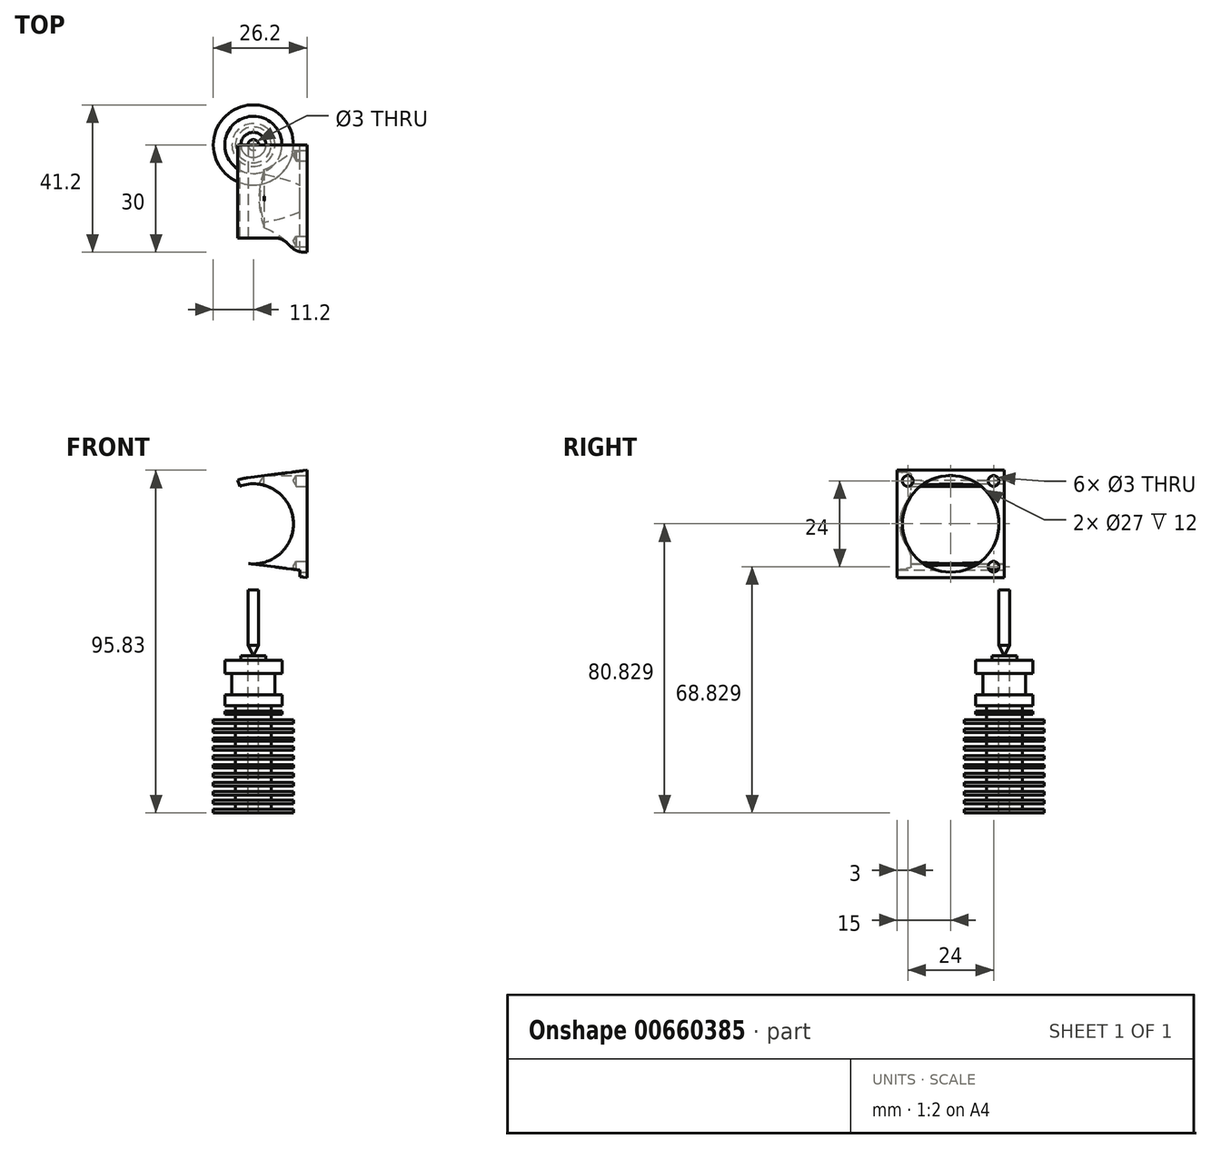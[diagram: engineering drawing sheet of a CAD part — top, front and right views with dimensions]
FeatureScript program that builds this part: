
annotation { "Feature Type Name" : "Feature", "Feature Type Description" : "" }
export const myFeature = defineFeature(function(context is Context, id is Id, definition is map)
    precondition{}
    {
        {
            var Q0;
            Q0=qCreatedBy(makeId("Front.planeOp"),FACE);
            var sketch = newSketch(context, id + "F0", { "sketchPlane" : qUnion([Q0])});
            skLineSegment(sketch, "E0.bottom", {"start": v(-3.5, 0) * mm, "end": v(3.5, 0) * mm});
            skLineSegment(sketch, "E0.top", {"start": v(-3.5, -1.2) * mm, "end": v(3.5, -1.2) * mm});
            skLineSegment(sketch, "E0.left", {"start": v(-3.5, 0) * mm, "end": v(-3.5, -1.2) * mm});
            skLineSegment(sketch, "E0.right", {"start": v(3.5, 0) * mm, "end": v(3.5, -1.2) * mm});
            skPoint(sketch, "E1", {"position": v(0, 0) * mm});
            skLineSegment(sketch, "E2", {"start": v(0, 5.65) * mm, "end": v(0, -51.62) * mm});
            skLineSegment(sketch, "E3.bottom", {"start": v(-8, -1.2) * mm, "end": v(8, -1.2) * mm});
            skLineSegment(sketch, "E3.top", {"start": v(-8, -4.9) * mm, "end": v(8, -4.9) * mm});
            skLineSegment(sketch, "E3.left", {"start": v(-8, -1.2) * mm, "end": v(-8, -4.9) * mm});
            skLineSegment(sketch, "E3.right", {"start": v(8, -1.2) * mm, "end": v(8, -4.9) * mm});
            skLineSegment(sketch, "E4.bottom", {"start": v(-8, -10.9) * mm, "end": v(8, -10.9) * mm});
            skLineSegment(sketch, "E4.top", {"start": v(-8, -13.9) * mm, "end": v(8, -13.9) * mm});
            skLineSegment(sketch, "E4.left", {"start": v(-8, -10.9) * mm, "end": v(-8, -13.9) * mm});
            skLineSegment(sketch, "E4.right", {"start": v(8, -10.9) * mm, "end": v(8, -13.9) * mm});
            skLineSegment(sketch, "E5.bottom", {"start": v(-6, -4.9) * mm, "end": v(6, -4.9) * mm});
            skLineSegment(sketch, "E5.top", {"start": v(-6, -10.9) * mm, "end": v(6, -10.9) * mm});
            skLineSegment(sketch, "E5.left", {"start": v(-6, -4.9) * mm, "end": v(-6, -10.9) * mm});
            skLineSegment(sketch, "E5.right", {"start": v(6, -4.9) * mm, "end": v(6, -10.9) * mm});
            skLineSegment(sketch, "E6.bottom", {"start": v(-11.2, -17.9) * mm, "end": v(11.2, -17.9) * mm});
            skLineSegment(sketch, "E6.top", {"start": v(-11.2, -18.9) * mm, "end": v(11.2, -18.9) * mm});
            skLineSegment(sketch, "E6.left", {"start": v(-11.2, -17.9) * mm, "end": v(-11.2, -18.9) * mm});
            skLineSegment(sketch, "E6.right", {"start": v(11.2, -17.9) * mm, "end": v(11.2, -18.9) * mm});
            skLineSegment(sketch, "E7.bottom", {"start": v(-8, -15.4) * mm, "end": v(8, -15.4) * mm});
            skLineSegment(sketch, "E7.top", {"start": v(-8, -16.4) * mm, "end": v(8, -16.4) * mm});
            skLineSegment(sketch, "E7.left", {"start": v(-8, -15.4) * mm, "end": v(-8, -16.4) * mm});
            skLineSegment(sketch, "E7.right", {"start": v(8, -15.4) * mm, "end": v(8, -16.4) * mm});
            skLineSegment(sketch, "E8.bottom", {"start": v(-5, -16.4) * mm, "end": v(5, -16.4) * mm});
            skLineSegment(sketch, "E8.top", {"start": v(-5, -43.9) * mm, "end": v(5, -43.9) * mm});
            skLineSegment(sketch, "E8.left", {"start": v(-5, -16.4) * mm, "end": v(-5, -43.9) * mm});
            skLineSegment(sketch, "E8.right", {"start": v(5, -16.4) * mm, "end": v(5, -43.9) * mm});
            skLineSegment(sketch, "E9.bottom", {"start": v(-5, -13.9) * mm, "end": v(5, -13.9) * mm});
            skLineSegment(sketch, "E9.top", {"start": v(-5, -15.4) * mm, "end": v(5, -15.4) * mm});
            skLineSegment(sketch, "E9.left", {"start": v(-5, -13.9) * mm, "end": v(-5, -15.4) * mm});
            skLineSegment(sketch, "E9.right", {"start": v(5, -13.9) * mm, "end": v(5, -15.4) * mm});
            skLineSegment(sketch, "E10", {"start": v(-23.04, -43.9) * mm, "end": v(22.42, -43.9) * mm, "construction": true});
            skLineSegment(sketch, "E11.bottom", {"start": v(-11.2, -42.9) * mm, "end": v(11.2, -42.9) * mm});
            skLineSegment(sketch, "E11.top", {"start": v(-11.2, -43.9) * mm, "end": v(11.2, -43.9) * mm});
            skLineSegment(sketch, "E11.left", {"start": v(-11.2, -42.9) * mm, "end": v(-11.2, -43.9) * mm});
            skLineSegment(sketch, "E11.right", {"start": v(11.2, -42.9) * mm, "end": v(11.2, -43.9) * mm});
            skLineSegment(sketch, "E12.bottom", {"start": v(-11.2, -40.4) * mm, "end": v(11.2, -40.4) * mm});
            skLineSegment(sketch, "E12.top", {"start": v(-11.2, -41.4) * mm, "end": v(11.2, -41.4) * mm});
            skLineSegment(sketch, "E12.left", {"start": v(-11.2, -40.4) * mm, "end": v(-11.2, -41.4) * mm});
            skLineSegment(sketch, "E12.right", {"start": v(11.2, -40.4) * mm, "end": v(11.2, -41.4) * mm});
            skLineSegment(sketch, "E13.bottom", {"start": v(-11.2, -37.9) * mm, "end": v(11.2, -37.9) * mm});
            skLineSegment(sketch, "E13.top", {"start": v(-11.2, -38.9) * mm, "end": v(11.2, -38.9) * mm});
            skLineSegment(sketch, "E13.left", {"start": v(-11.2, -37.9) * mm, "end": v(-11.2, -38.9) * mm});
            skLineSegment(sketch, "E13.right", {"start": v(11.2, -37.9) * mm, "end": v(11.2, -38.9) * mm});
            skLineSegment(sketch, "E14.bottom", {"start": v(-11.2, -35.4) * mm, "end": v(11.2, -35.4) * mm});
            skLineSegment(sketch, "E14.top", {"start": v(-11.2, -36.4) * mm, "end": v(11.2, -36.4) * mm});
            skLineSegment(sketch, "E14.left", {"start": v(-11.2, -35.4) * mm, "end": v(-11.2, -36.4) * mm});
            skLineSegment(sketch, "E14.right", {"start": v(11.2, -35.4) * mm, "end": v(11.2, -36.4) * mm});
            skLineSegment(sketch, "E15.bottom", {"start": v(-11.2, -32.9) * mm, "end": v(11.2, -32.9) * mm});
            skLineSegment(sketch, "E15.top", {"start": v(-11.2, -33.9) * mm, "end": v(11.2, -33.9) * mm});
            skLineSegment(sketch, "E15.left", {"start": v(-11.2, -32.9) * mm, "end": v(-11.2, -33.9) * mm});
            skLineSegment(sketch, "E15.right", {"start": v(11.2, -32.9) * mm, "end": v(11.2, -33.9) * mm});
            skLineSegment(sketch, "E16.bottom", {"start": v(-11.2, -30.4) * mm, "end": v(11.2, -30.4) * mm});
            skLineSegment(sketch, "E16.top", {"start": v(-11.2, -31.4) * mm, "end": v(11.2, -31.4) * mm});
            skLineSegment(sketch, "E16.left", {"start": v(-11.2, -30.4) * mm, "end": v(-11.2, -31.4) * mm});
            skLineSegment(sketch, "E16.right", {"start": v(11.2, -30.4) * mm, "end": v(11.2, -31.4) * mm});
            skLineSegment(sketch, "E17.bottom", {"start": v(-11.2, -27.9) * mm, "end": v(11.2, -27.9) * mm});
            skLineSegment(sketch, "E17.top", {"start": v(-11.2, -28.9) * mm, "end": v(11.2, -28.9) * mm});
            skLineSegment(sketch, "E17.left", {"start": v(-11.2, -27.9) * mm, "end": v(-11.2, -28.9) * mm});
            skLineSegment(sketch, "E17.right", {"start": v(11.2, -27.9) * mm, "end": v(11.2, -28.9) * mm});
            skLineSegment(sketch, "E18.bottom", {"start": v(-11.2, -25.4) * mm, "end": v(11.2, -25.4) * mm});
            skLineSegment(sketch, "E18.top", {"start": v(-11.2, -26.4) * mm, "end": v(11.2, -26.4) * mm});
            skLineSegment(sketch, "E18.left", {"start": v(-11.2, -25.4) * mm, "end": v(-11.2, -26.4) * mm});
            skLineSegment(sketch, "E18.right", {"start": v(11.2, -25.4) * mm, "end": v(11.2, -26.4) * mm});
            skLineSegment(sketch, "E19.bottom", {"start": v(-11.2, -22.9) * mm, "end": v(11.2, -22.9) * mm});
            skLineSegment(sketch, "E19.top", {"start": v(-11.2, -23.9) * mm, "end": v(11.2, -23.9) * mm});
            skLineSegment(sketch, "E19.left", {"start": v(-11.2, -22.9) * mm, "end": v(-11.2, -23.9) * mm});
            skLineSegment(sketch, "E19.right", {"start": v(11.2, -22.9) * mm, "end": v(11.2, -23.9) * mm});
            skLineSegment(sketch, "E20.bottom", {"start": v(-11.2, -20.4) * mm, "end": v(11.2, -20.4) * mm});
            skLineSegment(sketch, "E20.top", {"start": v(-11.2, -21.4) * mm, "end": v(11.2, -21.4) * mm});
            skLineSegment(sketch, "E20.left", {"start": v(-11.2, -20.4) * mm, "end": v(-11.2, -21.4) * mm});
            skLineSegment(sketch, "E20.right", {"start": v(11.2, -20.4) * mm, "end": v(11.2, -21.4) * mm});
            skLineSegment(sketch, "E21.bottom", {"start": v(29.22, -43.9) * mm, "end": v(59.22, -43.9) * mm});
            skLineSegment(sketch, "E21.top", {"start": v(29.22, -13.9) * mm, "end": v(59.22, -13.9) * mm});
            skLineSegment(sketch, "E21.left", {"start": v(29.22, -43.9) * mm, "end": v(29.22, -13.9) * mm});
            skLineSegment(sketch, "E21.right", {"start": v(59.22, -43.9) * mm, "end": v(59.22, -13.9) * mm});
            skLineSegment(sketch, "E22", {"start": v(87.52, -43.9) * mm, "end": v(112.52, -43.9) * mm});
            skLineSegment(sketch, "E23", {"start": v(112.52, -43.9) * mm, "end": v(112.52, -13.9) * mm});
            skLineSegment(sketch, "E24", {"start": v(112.52, -13.9) * mm, "end": v(102.52, -13.9) * mm});
            skLineSegment(sketch, "E25", {"start": v(102.52, -13.9) * mm, "end": v(102.52, -17.9) * mm});
            skLineSegment(sketch, "E26", {"start": v(102.52, -17.9) * mm, "end": v(87.52, -17.9) * mm});
            skLineSegment(sketch, "E27", {"start": v(87.52, -17.9) * mm, "end": v(87.52, -43.9) * mm});
            skCircle(sketch, "E28", {"center": v(0, 36.93) * mm, "radius": 11.2 * mm, "construction": true});
            skCircle(sketch, "E29", {"center": v(0, 36.93) * mm, "radius": 13 * mm, "construction": true});
            skLineSegment(sketch, "E30.right", {"start": v(25, 21.93) * mm, "end": v(25, 51.93) * mm});
            skLineSegment(sketch, "E31.right", {"start": v(15, 21.93) * mm, "end": v(15, 51.93) * mm});
            skLineSegment(sketch, "E32", {"start": v(15, 51.93) * mm, "end": v(-1.63, 49.83) * mm});
            skLineSegment(sketch, "E33", {"start": v(15, 21.93) * mm, "end": v(-1.63, 24.03) * mm});
            skLineSegment(sketch, "E34", {"start": v(15, 21.93) * mm, "end": v(25, 21.93) * mm});
            skLineSegment(sketch, "E35", {"start": v(15, 51.93) * mm, "end": v(25, 51.93) * mm});
            skLineSegment(sketch, "E36", {"start": v(0, 36.93) * mm, "end": v(-4.45, 49.15) * mm});
            skArc(sketch, "E37", {"start": v(-1.63, 49.83) * mm, "mid": v(-3.06, 49.56) * mm, "end": v(-4.45, 49.15) * mm});
            skPoint(sketch, "E38", {"position": v(15, 50.13) * mm});
            skPoint(sketch, "E39", {"position": v(15, 23.73) * mm});
            skLineSegment(sketch, "E40", {"start": v(15, 23.73) * mm, "end": v(-1.41, 25.82) * mm});
            skLineSegment(sketch, "E41", {"start": v(15, 50.13) * mm, "end": v(-1.41, 48.04) * mm});
            skLineSegment(sketch, "E42", {"start": v(0, 36.93) * mm, "end": v(-4.45, 24.71) * mm});
            skArc(sketch, "E43", {"start": v(-3.83, 47.45) * mm, "mid": v(11.2, 36.93) * mm, "end": v(-3.83, 26.4) * mm});
            skArc(sketch, "E44", {"start": v(-1.63, 24.03) * mm, "mid": v(-3.06, 24.3) * mm, "end": v(-4.45, 24.71) * mm});
            skLineSegment(sketch, "E45", {"start": v(0, 36.93) * mm, "end": v(33.8, 36.93) * mm, "construction": true});
            skLineSegment(sketch, "E46", {"start": v(13, 51.68) * mm, "end": v(13, 22.18) * mm});
            skSolve(sketch);
        }
        {
            var Q0;
            {var subQ0=sQuery(id+"F0.wireOp",EDGE,"E3.left");Q0=makeQuery(id+"F0.imprint","IMPRINT",FACE,{"disambiguationData":[TD([[makeQuery(id+"F0.imprint","IMPRINT",EDGE,{"derivedFrom":subQ0}),1.0]])]});}
            var Q1;
            {var subQ0=sQuery(id+"F0.wireOp",EDGE,"E0.left");Q1=makeQuery(id+"F0.imprint","IMPRINT",FACE,{"disambiguationData":[TD([[makeQuery(id+"F0.imprint","IMPRINT",EDGE,{"derivedFrom":subQ0}),1.0]])]});}
            var Q2;
            {var subQ5=sQuery(id+"F0.wireOp",EDGE,"E5.left");Q2=makeQuery(id+"F0.imprint","IMPRINT",FACE,{"disambiguationData":[TD([[makeQuery(id+"F0.imprint","IMPRINT",EDGE,{"derivedFrom":subQ5}),1.0]])]});}
            var Q3;
            {var subQ0=sQuery(id+"F0.wireOp",EDGE,"E4.left");Q3=makeQuery(id+"F0.imprint","IMPRINT",FACE,{"disambiguationData":[TD([[makeQuery(id+"F0.imprint","IMPRINT",EDGE,{"derivedFrom":subQ0}),1.0]])]});}
            var Q4;
            {var subQ5=sQuery(id+"F0.wireOp",EDGE,"E9.left");Q4=makeQuery(id+"F0.imprint","IMPRINT",FACE,{"disambiguationData":[TD([[makeQuery(id+"F0.imprint","IMPRINT",EDGE,{"derivedFrom":subQ5}),1.0]])]});}
            var Q5;
            {var subQ0=sQuery(id+"F0.wireOp",EDGE,"E7.left");Q5=makeQuery(id+"F0.imprint","IMPRINT",FACE,{"disambiguationData":[TD([[makeQuery(id+"F0.imprint","IMPRINT",EDGE,{"derivedFrom":subQ0}),1.0]])]});}
            var Q6;
            {var subQ0=sQuery(id+"F0.wireOp",EDGE,"E8.bottom");var subQ1=sQuery(id+"F0.wireOp",EDGE,"E2");var subQ2=makeQuery(id+"F0.imprint","INTERSECT",VERTEX,{"derivedFrom":[subQ1,subQ0]});Q6=makeQuery(id+"F0.imprint","IMPRINT",FACE,{"disambiguationData":[TD([[makeQuery(id+"F0.imprint","IMPRINT",EDGE,{"disambiguationData":[TD([[subQ2,-1.0]])],"derivedFrom":subQ1}),-1.0]])]});}
            var Q7;
            {var subQ0=sQuery(id+"F0.wireOp",EDGE,"E6.bottom");var subQ1=sQuery(id+"F0.wireOp",EDGE,"E2");var subQ2=makeQuery(id+"F0.imprint","INTERSECT",VERTEX,{"derivedFrom":[subQ1,subQ0]});Q7=makeQuery(id+"F0.imprint","IMPRINT",FACE,{"disambiguationData":[TD([[makeQuery(id+"F0.imprint","IMPRINT",EDGE,{"disambiguationData":[TD([[subQ2,-1.0]])],"derivedFrom":subQ1}),-1.0]])]});}
            var Q8;
            {var subQ0=sQuery(id+"F0.wireOp",EDGE,"E6.top");var subQ1=sQuery(id+"F0.wireOp",EDGE,"E2");var subQ2=makeQuery(id+"F0.imprint","INTERSECT",VERTEX,{"derivedFrom":[subQ1,subQ0]});Q8=makeQuery(id+"F0.imprint","IMPRINT",FACE,{"disambiguationData":[TD([[makeQuery(id+"F0.imprint","IMPRINT",EDGE,{"disambiguationData":[TD([[subQ2,-1.0]])],"derivedFrom":subQ1}),-1.0]])]});}
            var Q9;
            {var subQ0=sQuery(id+"F0.wireOp",EDGE,"E20.bottom");var subQ1=sQuery(id+"F0.wireOp",EDGE,"E2");var subQ2=makeQuery(id+"F0.imprint","INTERSECT",VERTEX,{"derivedFrom":[subQ1,subQ0]});Q9=makeQuery(id+"F0.imprint","IMPRINT",FACE,{"disambiguationData":[TD([[makeQuery(id+"F0.imprint","IMPRINT",EDGE,{"disambiguationData":[TD([[subQ2,-1.0]])],"derivedFrom":subQ1}),-1.0]])]});}
            var Q10;
            {var subQ0=sQuery(id+"F0.wireOp",EDGE,"E19.bottom");var subQ1=sQuery(id+"F0.wireOp",EDGE,"E2");var subQ2=makeQuery(id+"F0.imprint","INTERSECT",VERTEX,{"derivedFrom":[subQ1,subQ0]});Q10=makeQuery(id+"F0.imprint","IMPRINT",FACE,{"disambiguationData":[TD([[makeQuery(id+"F0.imprint","IMPRINT",EDGE,{"disambiguationData":[TD([[subQ2,-1.0]])],"derivedFrom":subQ1}),-1.0]])]});}
            var Q11;
            {var subQ5=sQuery(id+"F0.wireOp",EDGE,"E20.left");Q11=makeQuery(id+"F0.imprint","IMPRINT",FACE,{"disambiguationData":[TD([[makeQuery(id+"F0.imprint","IMPRINT",EDGE,{"derivedFrom":subQ5}),1.0]])]});}
            var Q12;
            {var subQ5=sQuery(id+"F0.wireOp",EDGE,"E19.left");Q12=makeQuery(id+"F0.imprint","IMPRINT",FACE,{"disambiguationData":[TD([[makeQuery(id+"F0.imprint","IMPRINT",EDGE,{"derivedFrom":subQ5}),1.0]])]});}
            var Q13;
            {var subQ5=sQuery(id+"F0.wireOp",EDGE,"E18.left");Q13=makeQuery(id+"F0.imprint","IMPRINT",FACE,{"disambiguationData":[TD([[makeQuery(id+"F0.imprint","IMPRINT",EDGE,{"derivedFrom":subQ5}),1.0]])]});}
            var Q14;
            {var subQ5=sQuery(id+"F0.wireOp",EDGE,"E17.left");Q14=makeQuery(id+"F0.imprint","IMPRINT",FACE,{"disambiguationData":[TD([[makeQuery(id+"F0.imprint","IMPRINT",EDGE,{"derivedFrom":subQ5}),1.0]])]});}
            var Q15;
            {var subQ5=sQuery(id+"F0.wireOp",EDGE,"E15.left");Q15=makeQuery(id+"F0.imprint","IMPRINT",FACE,{"disambiguationData":[TD([[makeQuery(id+"F0.imprint","IMPRINT",EDGE,{"derivedFrom":subQ5}),1.0]])]});}
            var Q16;
            {var subQ5=sQuery(id+"F0.wireOp",EDGE,"E16.left");Q16=makeQuery(id+"F0.imprint","IMPRINT",FACE,{"disambiguationData":[TD([[makeQuery(id+"F0.imprint","IMPRINT",EDGE,{"derivedFrom":subQ5}),1.0]])]});}
            var Q17;
            {var subQ5=sQuery(id+"F0.wireOp",EDGE,"E13.left");Q17=makeQuery(id+"F0.imprint","IMPRINT",FACE,{"disambiguationData":[TD([[makeQuery(id+"F0.imprint","IMPRINT",EDGE,{"derivedFrom":subQ5}),1.0]])]});}
            var Q18;
            {var subQ5=sQuery(id+"F0.wireOp",EDGE,"E12.left");Q18=makeQuery(id+"F0.imprint","IMPRINT",FACE,{"disambiguationData":[TD([[makeQuery(id+"F0.imprint","IMPRINT",EDGE,{"derivedFrom":subQ5}),1.0]])]});}
            var Q19;
            {var subQ5=sQuery(id+"F0.wireOp",EDGE,"E14.left");Q19=makeQuery(id+"F0.imprint","IMPRINT",FACE,{"disambiguationData":[TD([[makeQuery(id+"F0.imprint","IMPRINT",EDGE,{"derivedFrom":subQ5}),1.0]])]});}
            var Q20;
            {var subQ5=sQuery(id+"F0.wireOp",EDGE,"E11.left");Q20=makeQuery(id+"F0.imprint","IMPRINT",FACE,{"disambiguationData":[TD([[makeQuery(id+"F0.imprint","IMPRINT",EDGE,{"derivedFrom":subQ5}),1.0]])]});}
            var Q21;
            {var subQ0=sQuery(id+"F0.wireOp",EDGE,"E18.bottom");var subQ1=sQuery(id+"F0.wireOp",EDGE,"E2");var subQ2=makeQuery(id+"F0.imprint","INTERSECT",VERTEX,{"derivedFrom":[subQ1,subQ0]});Q21=makeQuery(id+"F0.imprint","IMPRINT",FACE,{"disambiguationData":[TD([[makeQuery(id+"F0.imprint","IMPRINT",EDGE,{"disambiguationData":[TD([[subQ2,-1.0]])],"derivedFrom":subQ1}),-1.0]])]});}
            var Q22;
            {var subQ0=sQuery(id+"F0.wireOp",EDGE,"E6.left");Q22=makeQuery(id+"F0.imprint","IMPRINT",FACE,{"disambiguationData":[TD([[makeQuery(id+"F0.imprint","IMPRINT",EDGE,{"derivedFrom":subQ0}),1.0]])]});}
            var Q23;
            {var subQ0=sQuery(id+"F0.wireOp",EDGE,"E18.top");var subQ1=sQuery(id+"F0.wireOp",EDGE,"E2");var subQ2=makeQuery(id+"F0.imprint","INTERSECT",VERTEX,{"derivedFrom":[subQ1,subQ0]});Q23=makeQuery(id+"F0.imprint","IMPRINT",FACE,{"disambiguationData":[TD([[makeQuery(id+"F0.imprint","IMPRINT",EDGE,{"disambiguationData":[TD([[subQ2,-1.0]])],"derivedFrom":subQ1}),-1.0]])]});}
            var Q24;
            {var subQ0=sQuery(id+"F0.wireOp",EDGE,"E19.top");var subQ1=sQuery(id+"F0.wireOp",EDGE,"E2");var subQ2=makeQuery(id+"F0.imprint","INTERSECT",VERTEX,{"derivedFrom":[subQ1,subQ0]});Q24=makeQuery(id+"F0.imprint","IMPRINT",FACE,{"disambiguationData":[TD([[makeQuery(id+"F0.imprint","IMPRINT",EDGE,{"disambiguationData":[TD([[subQ2,-1.0]])],"derivedFrom":subQ1}),-1.0]])]});}
            var Q25;
            {var subQ0=sQuery(id+"F0.wireOp",EDGE,"E20.top");var subQ1=sQuery(id+"F0.wireOp",EDGE,"E2");var subQ2=makeQuery(id+"F0.imprint","INTERSECT",VERTEX,{"derivedFrom":[subQ1,subQ0]});Q25=makeQuery(id+"F0.imprint","IMPRINT",FACE,{"disambiguationData":[TD([[makeQuery(id+"F0.imprint","IMPRINT",EDGE,{"disambiguationData":[TD([[subQ2,-1.0]])],"derivedFrom":subQ1}),-1.0]])]});}
            var Q26;
            {var subQ0=sQuery(id+"F0.wireOp",EDGE,"E12.top");var subQ1=sQuery(id+"F0.wireOp",EDGE,"E2");var subQ2=makeQuery(id+"F0.imprint","INTERSECT",VERTEX,{"derivedFrom":[subQ1,subQ0]});Q26=makeQuery(id+"F0.imprint","IMPRINT",FACE,{"disambiguationData":[TD([[makeQuery(id+"F0.imprint","IMPRINT",EDGE,{"disambiguationData":[TD([[subQ2,-1.0]])],"derivedFrom":subQ1}),-1.0]])]});}
            var Q27;
            {var subQ0=sQuery(id+"F0.wireOp",EDGE,"E13.top");var subQ1=sQuery(id+"F0.wireOp",EDGE,"E2");var subQ2=makeQuery(id+"F0.imprint","INTERSECT",VERTEX,{"derivedFrom":[subQ1,subQ0]});Q27=makeQuery(id+"F0.imprint","IMPRINT",FACE,{"disambiguationData":[TD([[makeQuery(id+"F0.imprint","IMPRINT",EDGE,{"disambiguationData":[TD([[subQ2,-1.0]])],"derivedFrom":subQ1}),-1.0]])]});}
            var Q28;
            {var subQ0=sQuery(id+"F0.wireOp",EDGE,"E17.top");var subQ1=sQuery(id+"F0.wireOp",EDGE,"E2");var subQ2=makeQuery(id+"F0.imprint","INTERSECT",VERTEX,{"derivedFrom":[subQ1,subQ0]});Q28=makeQuery(id+"F0.imprint","IMPRINT",FACE,{"disambiguationData":[TD([[makeQuery(id+"F0.imprint","IMPRINT",EDGE,{"disambiguationData":[TD([[subQ2,-1.0]])],"derivedFrom":subQ1}),-1.0]])]});}
            var Q29;
            {var subQ0=sQuery(id+"F0.wireOp",EDGE,"E16.top");var subQ1=sQuery(id+"F0.wireOp",EDGE,"E2");var subQ2=makeQuery(id+"F0.imprint","INTERSECT",VERTEX,{"derivedFrom":[subQ1,subQ0]});Q29=makeQuery(id+"F0.imprint","IMPRINT",FACE,{"disambiguationData":[TD([[makeQuery(id+"F0.imprint","IMPRINT",EDGE,{"disambiguationData":[TD([[subQ2,-1.0]])],"derivedFrom":subQ1}),-1.0]])]});}
            var Q30;
            {var subQ0=sQuery(id+"F0.wireOp",EDGE,"E14.top");var subQ1=sQuery(id+"F0.wireOp",EDGE,"E2");var subQ2=makeQuery(id+"F0.imprint","INTERSECT",VERTEX,{"derivedFrom":[subQ1,subQ0]});Q30=makeQuery(id+"F0.imprint","IMPRINT",FACE,{"disambiguationData":[TD([[makeQuery(id+"F0.imprint","IMPRINT",EDGE,{"disambiguationData":[TD([[subQ2,-1.0]])],"derivedFrom":subQ1}),-1.0]])]});}
            var Q31;
            {var subQ0=sQuery(id+"F0.wireOp",EDGE,"E17.bottom");var subQ1=sQuery(id+"F0.wireOp",EDGE,"E2");var subQ2=makeQuery(id+"F0.imprint","INTERSECT",VERTEX,{"derivedFrom":[subQ1,subQ0]});Q31=makeQuery(id+"F0.imprint","IMPRINT",FACE,{"disambiguationData":[TD([[makeQuery(id+"F0.imprint","IMPRINT",EDGE,{"disambiguationData":[TD([[subQ2,-1.0]])],"derivedFrom":subQ1}),-1.0]])]});}
            var Q32;
            {var subQ0=sQuery(id+"F0.wireOp",EDGE,"E16.bottom");var subQ1=sQuery(id+"F0.wireOp",EDGE,"E2");var subQ2=makeQuery(id+"F0.imprint","INTERSECT",VERTEX,{"derivedFrom":[subQ1,subQ0]});Q32=makeQuery(id+"F0.imprint","IMPRINT",FACE,{"disambiguationData":[TD([[makeQuery(id+"F0.imprint","IMPRINT",EDGE,{"disambiguationData":[TD([[subQ2,-1.0]])],"derivedFrom":subQ1}),-1.0]])]});}
            var Q33;
            {var subQ0=sQuery(id+"F0.wireOp",EDGE,"E15.bottom");var subQ1=sQuery(id+"F0.wireOp",EDGE,"E2");var subQ2=makeQuery(id+"F0.imprint","INTERSECT",VERTEX,{"derivedFrom":[subQ1,subQ0]});Q33=makeQuery(id+"F0.imprint","IMPRINT",FACE,{"disambiguationData":[TD([[makeQuery(id+"F0.imprint","IMPRINT",EDGE,{"disambiguationData":[TD([[subQ2,-1.0]])],"derivedFrom":subQ1}),-1.0]])]});}
            var Q34;
            {var subQ0=sQuery(id+"F0.wireOp",EDGE,"E12.bottom");var subQ1=sQuery(id+"F0.wireOp",EDGE,"E2");var subQ2=makeQuery(id+"F0.imprint","INTERSECT",VERTEX,{"derivedFrom":[subQ1,subQ0]});Q34=makeQuery(id+"F0.imprint","IMPRINT",FACE,{"disambiguationData":[TD([[makeQuery(id+"F0.imprint","IMPRINT",EDGE,{"disambiguationData":[TD([[subQ2,-1.0]])],"derivedFrom":subQ1}),-1.0]])]});}
            var Q35;
            {var subQ0=sQuery(id+"F0.wireOp",EDGE,"E13.bottom");var subQ1=sQuery(id+"F0.wireOp",EDGE,"E2");var subQ2=makeQuery(id+"F0.imprint","INTERSECT",VERTEX,{"derivedFrom":[subQ1,subQ0]});Q35=makeQuery(id+"F0.imprint","IMPRINT",FACE,{"disambiguationData":[TD([[makeQuery(id+"F0.imprint","IMPRINT",EDGE,{"disambiguationData":[TD([[subQ2,-1.0]])],"derivedFrom":subQ1}),-1.0]])]});}
            var Q36;
            {var subQ0=sQuery(id+"F0.wireOp",EDGE,"E15.top");var subQ1=sQuery(id+"F0.wireOp",EDGE,"E2");var subQ2=makeQuery(id+"F0.imprint","INTERSECT",VERTEX,{"derivedFrom":[subQ1,subQ0]});Q36=makeQuery(id+"F0.imprint","IMPRINT",FACE,{"disambiguationData":[TD([[makeQuery(id+"F0.imprint","IMPRINT",EDGE,{"disambiguationData":[TD([[subQ2,-1.0]])],"derivedFrom":subQ1}),-1.0]])]});}
            var Q37;
            {var subQ0=sQuery(id+"F0.wireOp",EDGE,"E14.bottom");var subQ1=sQuery(id+"F0.wireOp",EDGE,"E2");var subQ2=makeQuery(id+"F0.imprint","INTERSECT",VERTEX,{"derivedFrom":[subQ1,subQ0]});Q37=makeQuery(id+"F0.imprint","IMPRINT",FACE,{"disambiguationData":[TD([[makeQuery(id+"F0.imprint","IMPRINT",EDGE,{"disambiguationData":[TD([[subQ2,-1.0]])],"derivedFrom":subQ1}),-1.0]])]});}
            var Q38;
            {var subQ0=sQuery(id+"F0.wireOp",EDGE,"E11.top");var subQ1=sQuery(id+"F0.wireOp",EDGE,"E2");var subQ2=makeQuery(id+"F0.imprint","INTERSECT",VERTEX,{"derivedFrom":[subQ1,subQ0]});Q38=makeQuery(id+"F0.imprint","IMPRINT",FACE,{"disambiguationData":[TD([[makeQuery(id+"F0.imprint","IMPRINT",EDGE,{"disambiguationData":[TD([[subQ2,1.0]])],"derivedFrom":subQ1}),-1.0]])]});}
            var Q39;
            Q39=sQuery(id+"F0.wireOp",EDGE,"E2");
            revolve(context, id + "F1", {"entities" : qUnion([Q0, Q1, Q2, Q3, Q4, Q5, Q6, Q7, Q8, Q9, Q10, Q11, Q12, Q13, Q14, Q15, Q16, Q17, Q18, Q19, Q20, Q21, Q22, Q23, Q24, Q25, Q26, Q27, Q28, Q29, Q30, Q31, Q32, Q33, Q34, Q35, Q36, Q37, Q38]), "axis" : qUnion([Q39]), "revolveType" : RevolveType.FULL});
        }
        {
            var Q0;
            Q0=makeQuery(id+"F1.opRevolve","SWEPT_FACE",FACE,{"disambiguationData":[OSD([sQuery(id+"F0.wireOp",EDGE,"E0.bottom")])]});
            var sketch = newSketch(context, id + "F2", { "sketchPlane" : qUnion([Q0])});
            skPoint(sketch, "E47", {"position": v(0, 0) * mm});
            skSolve(sketch);
        }
        {
            var Q0;
            Q0=sQuery(id+"F2.wireOp",VERTEX,"E47");
            var Q1;
            Q1=makeQuery(id+"F1.opRevolve","SWEPT_BODY",BODY,{"disambiguationData":[OSD([sQuery(id+"F0.wireOp",EDGE,"E0.bottom"),sQuery(id+"F0.wireOp",EDGE,"E0.left"),sQuery(id+"F0.wireOp",EDGE,"E2"),sQuery(id+"F0.wireOp",EDGE,"E3.bottom"),sQuery(id+"F0.wireOp",EDGE,"E3.top"),sQuery(id+"F0.wireOp",EDGE,"E3.left"),sQuery(id+"F0.wireOp",EDGE,"E4.bottom"),sQuery(id+"F0.wireOp",EDGE,"E4.top"),sQuery(id+"F0.wireOp",EDGE,"E4.left"),sQuery(id+"F0.wireOp",EDGE,"E5.left"),sQuery(id+"F0.wireOp",EDGE,"E6.bottom"),sQuery(id+"F0.wireOp",EDGE,"E6.top"),sQuery(id+"F0.wireOp",EDGE,"E6.left"),sQuery(id+"F0.wireOp",EDGE,"E7.bottom"),sQuery(id+"F0.wireOp",EDGE,"E7.top"),sQuery(id+"F0.wireOp",EDGE,"E7.left"),sQuery(id+"F0.wireOp",EDGE,"E8.left"),sQuery(id+"F0.wireOp",EDGE,"E9.left"),sQuery(id+"F0.wireOp",EDGE,"E11.bottom"),sQuery(id+"F0.wireOp",EDGE,"E11.top"),sQuery(id+"F0.wireOp",EDGE,"E11.left"),sQuery(id+"F0.wireOp",EDGE,"E12.bottom"),sQuery(id+"F0.wireOp",EDGE,"E12.top"),sQuery(id+"F0.wireOp",EDGE,"E12.left"),sQuery(id+"F0.wireOp",EDGE,"E13.bottom"),sQuery(id+"F0.wireOp",EDGE,"E13.top"),sQuery(id+"F0.wireOp",EDGE,"E13.left"),sQuery(id+"F0.wireOp",EDGE,"E14.bottom"),sQuery(id+"F0.wireOp",EDGE,"E14.top"),sQuery(id+"F0.wireOp",EDGE,"E14.left"),sQuery(id+"F0.wireOp",EDGE,"E15.bottom"),sQuery(id+"F0.wireOp",EDGE,"E15.top"),sQuery(id+"F0.wireOp",EDGE,"E15.left"),sQuery(id+"F0.wireOp",EDGE,"E16.bottom"),sQuery(id+"F0.wireOp",EDGE,"E16.top"),sQuery(id+"F0.wireOp",EDGE,"E16.left"),sQuery(id+"F0.wireOp",EDGE,"E17.bottom"),sQuery(id+"F0.wireOp",EDGE,"E17.top"),sQuery(id+"F0.wireOp",EDGE,"E17.left"),sQuery(id+"F0.wireOp",EDGE,"E18.bottom"),sQuery(id+"F0.wireOp",EDGE,"E18.top"),sQuery(id+"F0.wireOp",EDGE,"E18.left"),sQuery(id+"F0.wireOp",EDGE,"E19.bottom"),sQuery(id+"F0.wireOp",EDGE,"E19.top"),sQuery(id+"F0.wireOp",EDGE,"E19.left"),sQuery(id+"F0.wireOp",EDGE,"E20.bottom"),sQuery(id+"F0.wireOp",EDGE,"E20.top"),sQuery(id+"F0.wireOp",EDGE,"E20.left")])]});
            hole(context, id + "F3", {"style" : HoleStyle.SIMPLE, "endStyle" : HoleEndStyle.THROUGH, "holeDiameter" : 3 * mm, "majorDiameter" : 5 * mm, "isTappedThrough" : true, "tappedDepth" : 12 * mm, "tapClearance" : 3, "locations" : qUnion([Q0]), "scope" : qUnion([Q1])});
        }
        {
            var Q0;
            {var subQ0=sQuery(id+"F0.wireOp",EDGE,"E40");Q0=makeQuery(id+"F0.imprint","IMPRINT",FACE,{"disambiguationData":[TD([[makeQuery(id+"F0.imprint","IMPRINT",EDGE,{"derivedFrom":subQ0}),-1.0]])]});}
            var Q1;
            {var subQ4=sQuery(id+"F0.wireOp",EDGE,"E32");Q1=makeQuery(id+"F0.imprint","IMPRINT",FACE,{"disambiguationData":[TD([[makeQuery(id+"F0.imprint","IMPRINT",EDGE,{"derivedFrom":subQ4}),1.0]])]});}
            var Q2;
            {var subQ4=sQuery(id+"F0.wireOp",EDGE,"E33");Q2=makeQuery(id+"F0.imprint","IMPRINT",FACE,{"disambiguationData":[TD([[makeQuery(id+"F0.imprint","IMPRINT",EDGE,{"derivedFrom":subQ4}),-1.0]])]});}
            var Q3;
            {var subQ0=sQuery(id+"F0.wireOp",EDGE,"E37");Q3=makeQuery(id+"F0.imprint","IMPRINT",FACE,{"disambiguationData":[TD([[makeQuery(id+"F0.imprint","IMPRINT",EDGE,{"derivedFrom":subQ0}),1.0]])]});}
            var Q4;
            {var subQ5=sQuery(id+"F0.wireOp",EDGE,"E44");Q4=makeQuery(id+"F0.imprint","IMPRINT",FACE,{"disambiguationData":[TD([[makeQuery(id+"F0.imprint","IMPRINT",EDGE,{"derivedFrom":subQ5}),-1.0]])]});}
            extrude(context, id + "F4", {"entities" : qUnion([Q0, Q1, Q2, Q3, Q4]), "depth" : 26 * mm, "offsetDistance" : 25 * mm});
        }
        {
            var Q0;
            {var subQ5=sQuery(id+"F0.wireOp",EDGE,"E46");Q0=makeQuery(id+"F0.imprint","IMPRINT",FACE,{"disambiguationData":[TD([[makeQuery(id+"F0.imprint","IMPRINT",EDGE,{"derivedFrom":subQ5}),1.0]])]});}
            extrude(context, id + "F5", {"entities" : qUnion([Q0]), "operationType" : NewBodyOperationType.ADD, "depth" : 30 * mm, "offsetDistance" : 25 * mm});
        }
        {
            var Q0;
            Q0=makeQuery(id+"F5.boolean.opBoolean","INTERSECT",EDGE,{"derivedFrom":[makeQuery(id+"F4.opExtrude","CAP_FACE",FACE,{"disambiguationData":[OSD([sQuery(id+"F0.wireOp",EDGE,"E31.right"),sQuery(id+"F0.wireOp",EDGE,"E32"),sQuery(id+"F0.wireOp",EDGE,"E33"),sQuery(id+"F0.wireOp",EDGE,"E36"),sQuery(id+"F0.wireOp",EDGE,"E37"),sQuery(id+"F0.wireOp",EDGE,"E42"),sQuery(id+"F0.wireOp",EDGE,"E43"),sQuery(id+"F0.wireOp",EDGE,"E44")])],"isStart":false}),makeQuery(id+"F5.opExtrude","SWEPT_FACE",FACE,{"disambiguationData":[OSD([sQuery(id+"F0.wireOp",EDGE,"E46")])]})]});
            chamfer(context, id + "F6", {"entities" : qUnion([Q0]), "width" : 5 * mm, "tangentPropagation" : true});
        }
        {
            var Q0;
            {var subQ0=makeQuery(id+"F4.opExtrude","CAP_FACE",FACE,{"disambiguationData":[OSD([sQuery(id+"F0.wireOp",EDGE,"E31.right"),sQuery(id+"F0.wireOp",EDGE,"E32"),sQuery(id+"F0.wireOp",EDGE,"E33"),sQuery(id+"F0.wireOp",EDGE,"E36"),sQuery(id+"F0.wireOp",EDGE,"E37"),sQuery(id+"F0.wireOp",EDGE,"E42"),sQuery(id+"F0.wireOp",EDGE,"E43"),sQuery(id+"F0.wireOp",EDGE,"E44")])],"isStart":false});Q0=makeQuery(id+"F6.opChamfer","BLEND_EDGE",EDGE,{"disambiguationData":[OD(0.0)],"blendedFrom":[makeQuery(id+"F5.boolean.opBoolean","INTERSECT",EDGE,{"derivedFrom":[subQ0,makeQuery(id+"F5.opExtrude","SWEPT_FACE",FACE,{"disambiguationData":[OSD([sQuery(id+"F0.wireOp",EDGE,"E46")])]})]}),subQ0],"blendedInto":[subQ0]});}
            var Q1;
            {var subQ0=makeQuery(id+"F4.opExtrude","CAP_FACE",FACE,{"disambiguationData":[OSD([sQuery(id+"F0.wireOp",EDGE,"E31.right"),sQuery(id+"F0.wireOp",EDGE,"E32"),sQuery(id+"F0.wireOp",EDGE,"E33"),sQuery(id+"F0.wireOp",EDGE,"E36"),sQuery(id+"F0.wireOp",EDGE,"E37"),sQuery(id+"F0.wireOp",EDGE,"E42"),sQuery(id+"F0.wireOp",EDGE,"E43"),sQuery(id+"F0.wireOp",EDGE,"E44")])],"isStart":false});Q1=makeQuery(id+"F6.opChamfer","BLEND_EDGE",EDGE,{"disambiguationData":[OD(1.0)],"blendedFrom":[makeQuery(id+"F5.boolean.opBoolean","INTERSECT",EDGE,{"derivedFrom":[subQ0,makeQuery(id+"F5.opExtrude","SWEPT_FACE",FACE,{"disambiguationData":[OSD([sQuery(id+"F0.wireOp",EDGE,"E46")])]})]}),subQ0],"blendedInto":[subQ0]});}
            var Q2;
            {var subQ0=sQuery(id+"F0.wireOp",EDGE,"E46");var subQ1=sQuery(id+"F0.wireOp",EDGE,"E33");var subQ2=sQuery(id+"F0.wireOp",EDGE,"E32");var subQ3=sQuery(id+"F0.wireOp",EDGE,"E31.right");Q2=makeQuery(id+"F6.opChamfer","BLEND_EDGE",EDGE,{"blendedFrom":[makeQuery(id+"F5.boolean.opBoolean","INTERSECT",EDGE,{"derivedFrom":[makeQuery(id+"F4.opExtrude","CAP_FACE",FACE,{"disambiguationData":[OSD([subQ3,subQ2,subQ1,sQuery(id+"F0.wireOp",EDGE,"E36"),sQuery(id+"F0.wireOp",EDGE,"E37"),sQuery(id+"F0.wireOp",EDGE,"E42"),sQuery(id+"F0.wireOp",EDGE,"E43"),sQuery(id+"F0.wireOp",EDGE,"E44")])],"isStart":false}),makeQuery(id+"F5.opExtrude","SWEPT_FACE",FACE,{"disambiguationData":[OSD([subQ0])]})]}),makeQuery(id+"F5.opExtrude","CAP_FACE",FACE,{"disambiguationData":[OSD([subQ3,subQ2,subQ1,subQ0])],"isStart":false})],"blendedInto":[makeQuery(id+"F5.opExtrude","CAP_FACE",FACE,{"disambiguationData":[OSD([subQ3,subQ2,subQ1,subQ0])],"isStart":false})]});}
            fillet(context, id + "F7", {"entities" : qUnion([Q0, Q1, Q2]), "radius" : 5 * mm, "tangentPropagation" : true, "allowEdgeOverflow" : false});
        }
        {
            var Q0;
            {var subQ0=sQuery(id+"F0.wireOp",EDGE,"E31.right");Q0=makeQuery(id+"F5.boolean.opBoolean","MERGE",FACE,{"derivedFrom":[makeQuery(id+"F4.opExtrude","SWEPT_FACE",FACE,{"disambiguationData":[OSD([subQ0])]}),makeQuery(id+"F5.opExtrude","SWEPT_FACE",FACE,{"disambiguationData":[OSD([subQ0])]})]});}
            var sketch = newSketch(context, id + "F8", { "sketchPlane" : qUnion([Q0])});
            skLineSegment(sketch, "E48", {"start": v(-30, 51.93) * mm, "end": v(0, 21.93) * mm, "construction": true});
            skPoint(sketch, "E49", {"position": v(-15, 36.93) * mm});
            skLineSegment(sketch, "E50.bottom", {"start": v(-30, 51.93) * mm, "end": v(0, 51.93) * mm, "construction": true});
            skLineSegment(sketch, "E50.top", {"start": v(-30, 21.93) * mm, "end": v(0, 21.93) * mm, "construction": true});
            skLineSegment(sketch, "E50.left", {"start": v(-30, 51.93) * mm, "end": v(-30, 21.93) * mm, "construction": true});
            skLineSegment(sketch, "E50.right", {"start": v(0, 51.93) * mm, "end": v(0, 21.93) * mm, "construction": true});
            skPoint(sketch, "E51", {"position": v(-27, 48.93) * mm});
            skPoint(sketch, "E52", {"position": v(-3, 24.93) * mm});
            skPoint(sketch, "E53", {"position": v(-3, 48.93) * mm});
            skSolve(sketch);
        }
        {
            var Q0;
            Q0=qCreatedBy(makeId("Front.planeOp"),FACE);
            var sketch = newSketch(context, id + "F9", { "sketchPlane" : qUnion([Q0])});
            skLineSegment(sketch, "E54", {"start": v(0, 0) * mm, "end": v(0, 18.4) * mm});
            skLineSegment(sketch, "E55", {"start": v(-1.5, 0) * mm, "end": v(-1.5, 18.4) * mm});
            skLineSegment(sketch, "E56", {"start": v(1.5, 0) * mm, "end": v(1.5, 18.4) * mm});
            skLineSegment(sketch, "E57", {"start": v(-1.5, 18.4) * mm, "end": v(1.5, 18.4) * mm});
            skLineSegment(sketch, "E58", {"start": v(-1.5, 3) * mm, "end": v(1.5, 3) * mm});
            skLineSegment(sketch, "E59", {"start": v(-1.5, 3) * mm, "end": v(0, 0) * mm});
            skLineSegment(sketch, "E60", {"start": v(1.5, 3) * mm, "end": v(0, 0) * mm});
            skSolve(sketch);
        }
        {
            var Q0;
            {var subQ0=sQuery(id+"F9.wireOp",EDGE,"E57");var subQ1=sQuery(id+"F9.wireOp",EDGE,"E54");var subQ2=makeQuery(id+"F9.imprint","INTERSECT",VERTEX,{"derivedFrom":[subQ1,subQ0]});Q0=makeQuery(id+"F9.imprint","IMPRINT",FACE,{"disambiguationData":[TD([[makeQuery(id+"F9.imprint","IMPRINT",EDGE,{"disambiguationData":[TD([[subQ2,1.0]])],"derivedFrom":subQ1}),1.0]])]});}
            var Q1;
            {var subQ0=sQuery(id+"F9.wireOp",EDGE,"E59");Q1=makeQuery(id+"F9.imprint","IMPRINT",FACE,{"disambiguationData":[TD([[makeQuery(id+"F9.imprint","IMPRINT",EDGE,{"derivedFrom":subQ0}),1.0]])]});}
            var Q2;
            Q2=sQuery(id+"F9.wireOp",EDGE,"E54");
            revolve(context, id + "F10", {"entities" : qUnion([Q0, Q1]), "axis" : qUnion([Q2]), "revolveType" : RevolveType.FULL});
        }
        {
            var Q0;
            Q0=sQuery(id+"F8.wireOp",VERTEX,"E51");
            var Q1;
            Q1=sQuery(id+"F8.wireOp",VERTEX,"E52");
            var Q2;
            Q2=sQuery(id+"F8.wireOp",VERTEX,"E53");
            var Q3;
            Q3=makeQuery(id+"F4.opExtrude","SWEPT_BODY",BODY,{"disambiguationData":[OSD([sQuery(id+"F0.wireOp",EDGE,"E31.right"),sQuery(id+"F0.wireOp",EDGE,"E32"),sQuery(id+"F0.wireOp",EDGE,"E33"),sQuery(id+"F0.wireOp",EDGE,"E36"),sQuery(id+"F0.wireOp",EDGE,"E37"),sQuery(id+"F0.wireOp",EDGE,"E42"),sQuery(id+"F0.wireOp",EDGE,"E43"),sQuery(id+"F0.wireOp",EDGE,"E44")])]});
            hole(context, id + "F11", {"style" : HoleStyle.SIMPLE, "endStyle" : HoleEndStyle.BLIND, "holeDiameter" : 3 * mm, "majorDiameter" : 5 * mm, "holeDepth" : 3 * mm, "isTappedThrough" : true, "tappedDepth" : 12 * mm, "tapClearance" : 3, "locations" : qUnion([Q0, Q1, Q2]), "scope" : qUnion([Q3])});
        }
        {
            var Q0;
            Q0=sQuery(id+"F8.wireOp",VERTEX,"E49");
            var Q1;
            Q1=makeQuery(id+"F4.opExtrude","SWEPT_BODY",BODY,{"disambiguationData":[OSD([sQuery(id+"F0.wireOp",EDGE,"E31.right"),sQuery(id+"F0.wireOp",EDGE,"E32"),sQuery(id+"F0.wireOp",EDGE,"E33"),sQuery(id+"F0.wireOp",EDGE,"E36"),sQuery(id+"F0.wireOp",EDGE,"E37"),sQuery(id+"F0.wireOp",EDGE,"E42"),sQuery(id+"F0.wireOp",EDGE,"E43"),sQuery(id+"F0.wireOp",EDGE,"E44")])]});
            hole(context, id + "F12", {"style" : HoleStyle.SIMPLE, "endStyle" : HoleEndStyle.BLIND, "holeDiameter" : 27 * mm, "majorDiameter" : 5 * mm, "holeDepth" : 12 * mm, "isTappedThrough" : true, "tappedDepth" : 12 * mm, "tapClearance" : 3, "locations" : qUnion([Q0]), "scope" : qUnion([Q1])});
        }
        {
            var Q0;
            Q0=makeQuery(id+"F4.opExtrude","SWEPT_BODY",BODY,{"disambiguationData":[OSD([sQuery(id+"F0.wireOp",EDGE,"E31.right"),sQuery(id+"F0.wireOp",EDGE,"E32"),sQuery(id+"F0.wireOp",EDGE,"E33"),sQuery(id+"F0.wireOp",EDGE,"E36"),sQuery(id+"F0.wireOp",EDGE,"E37"),sQuery(id+"F0.wireOp",EDGE,"E42"),sQuery(id+"F0.wireOp",EDGE,"E43"),sQuery(id+"F0.wireOp",EDGE,"E44")])]});
            transform(context, id + "F13", {"entities" : qUnion([Q0]), "transformType" : TransformType.COPY});
        }
    });
